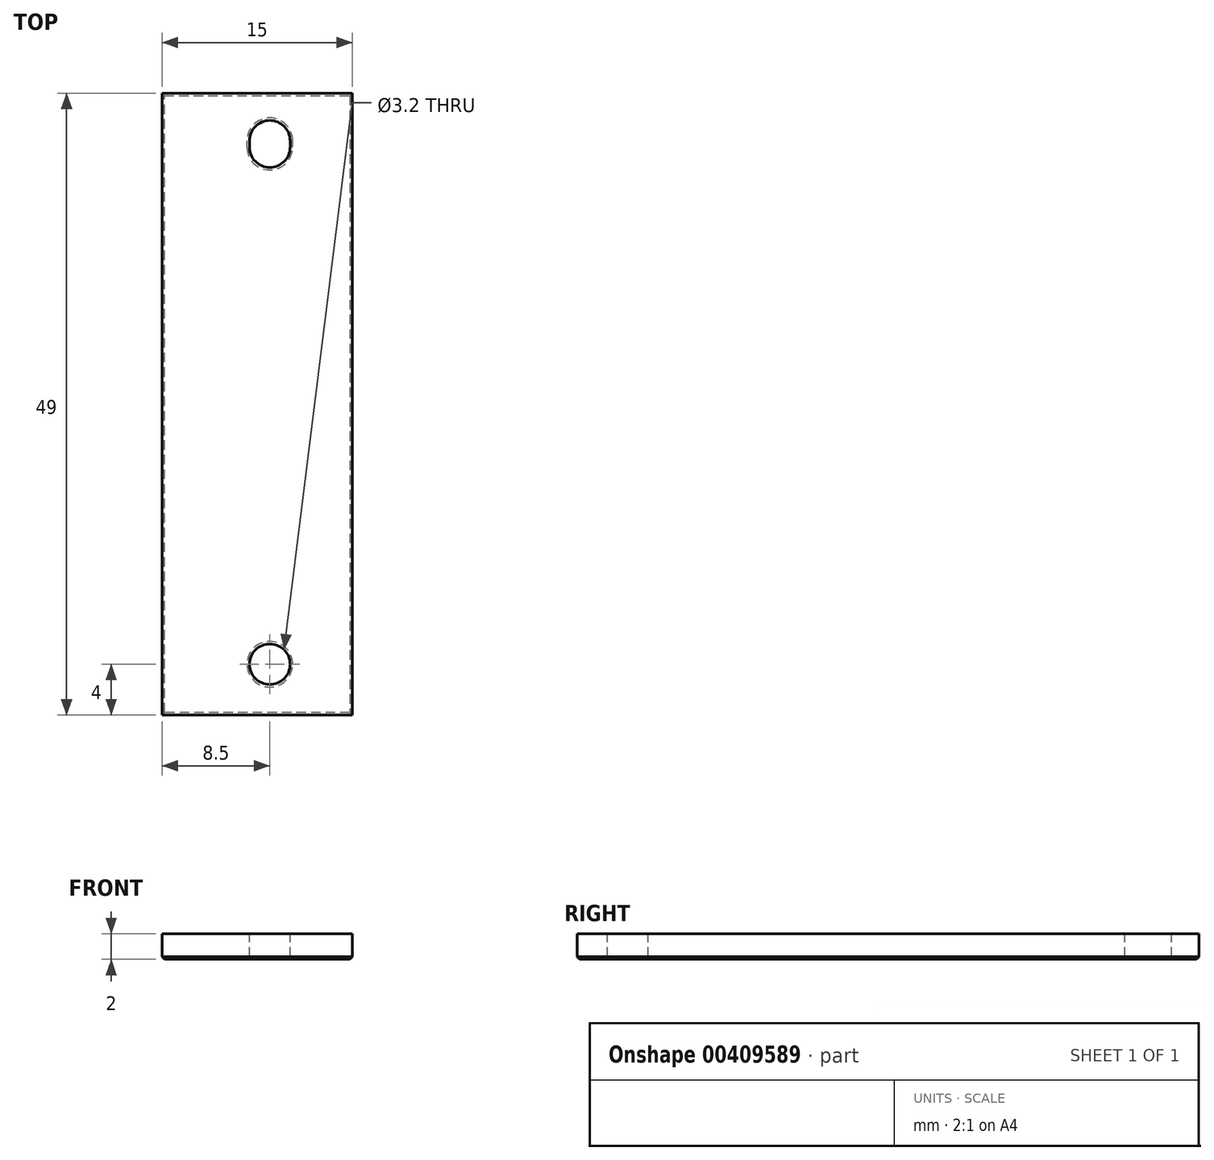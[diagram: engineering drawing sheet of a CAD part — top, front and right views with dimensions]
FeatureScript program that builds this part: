
annotation { "Feature Type Name" : "Feature", "Feature Type Description" : "" }
export const myFeature = defineFeature(function(context is Context, id is Id, definition is map)
    precondition{}
    {
        {
            var Q0;
            Q0=qCreatedBy(makeId("Top.planeOp"),FACE);
            var sketch = newSketch(context, id + "F0", { "sketchPlane" : qUnion([Q0])});
            skLineSegment(sketch, "E0.bottom", {"start": v(6.5, 24.5) * mm, "end": v(-8.5, 24.5) * mm});
            skLineSegment(sketch, "E0.top", {"start": v(6.5, -24.5) * mm, "end": v(-8.5, -24.5) * mm});
            skLineSegment(sketch, "E0.left", {"start": v(6.5, 24.5) * mm, "end": v(6.5, -24.5) * mm});
            skLineSegment(sketch, "E0.right", {"start": v(-8.5, 24.5) * mm, "end": v(-8.5, -24.5) * mm});
            skPoint(sketch, "E0.middle", {"position": v(0, 0) * mm});
            skLineSegment(sketch, "E1", {"start": v(0, 20.5) * mm, "end": v(0, -20.5) * mm, "construction": true});
            skCircle(sketch, "E2", {"center": v(0, -20.5) * mm, "radius": 1.6 * mm});
            skLineSegment(sketch, "E3", {"start": v(0, 20.75) * mm, "end": v(0, 20.25) * mm, "construction": true});
            skArc(sketch, "E4.0.startCap", {"start": v(-1.6, 20.75) * mm, "mid": v(0, 22.35) * mm, "end": v(1.6, 20.75) * mm});
            skArc(sketch, "E4.0.endCap", {"start": v(1.6, 20.25) * mm, "mid": v(0, 18.65) * mm, "end": v(-1.6, 20.25) * mm});
            skLineSegment(sketch, "E4.0.left", {"start": v(1.6, 20.75) * mm, "end": v(1.6, 20.25) * mm});
            skLineSegment(sketch, "E4.0.right", {"start": v(-1.6, 20.75) * mm, "end": v(-1.6, 20.25) * mm});
            skSolve(sketch);
        }
        {
            var Q0;
            Q0=qCreatedBy(makeId("Front.planeOp"),FACE);
            var sketch = newSketch(context, id + "F1", { "sketchPlane" : qUnion([Q0])});
            skLineSegment(sketch, "E5", {"start": v(0, 0) * mm, "end": v(0, 2) * mm});
            skSolve(sketch);
        }
        {
            var Q0;
            Q0=qSketchRegion(id+"F0",true);
            var Q1;
            Q1=sQuery(id+"F1.wireOp",EDGE,"E5");
            sweep(context, id + "F2", {"profiles" : qUnion([Q0]), "path" : qUnion([Q1])});
        }
        {
            var Q0;
            Q0=makeQuery(id+"F2.opSweep","CAP_FACE",FACE,{"disambiguationData":[OSD([sQuery(id+"F0.wireOp",EDGE,"E0.bottom"),sQuery(id+"F0.wireOp",EDGE,"E0.top"),sQuery(id+"F0.wireOp",EDGE,"E0.left"),sQuery(id+"F0.wireOp",EDGE,"E0.right"),sQuery(id+"F0.wireOp",EDGE,"E2"),sQuery(id+"F0.wireOp",EDGE,"E4.0.startCap"),sQuery(id+"F0.wireOp",EDGE,"E4.0.endCap"),sQuery(id+"F0.wireOp",EDGE,"E4.0.left"),sQuery(id+"F0.wireOp",EDGE,"E4.0.right"),sQuery(id+"F1.wireOp",VERTEX,"E5.start")])],"isStart":true});
            chamfer(context, id + "F3", {"entities" : qUnion([Q0]), "width" : 0.2 * mm});
        }
    });
